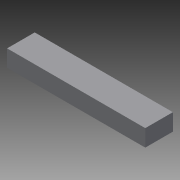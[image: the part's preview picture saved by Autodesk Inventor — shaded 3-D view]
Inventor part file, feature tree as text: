
AUTODESK INVENTOR PART (.ipt)
format: ipt  version: 2014 SP1 (Build 180222100, 222)  size: 67,584 bytes
history: native  units: in
note: dims shown in document units (in); Inventor stores cm internally (conversion verified against a paired STEP export)
features: extrude x1, sketch x1
ambient origin geometry x8: Origin, YZ Plane, XZ Plane, XY Plane, X Axis, Y Axis, Z Axis, Center Point
bodies: Solid1 (feature_tree)
feature tree (2):
  extrude  "Extrusion1"  Depth=0.61in
  sketch  "Sketch1"  dims[d0=1.0in d1=0.61in d2=5.0in d3=0.0in]
